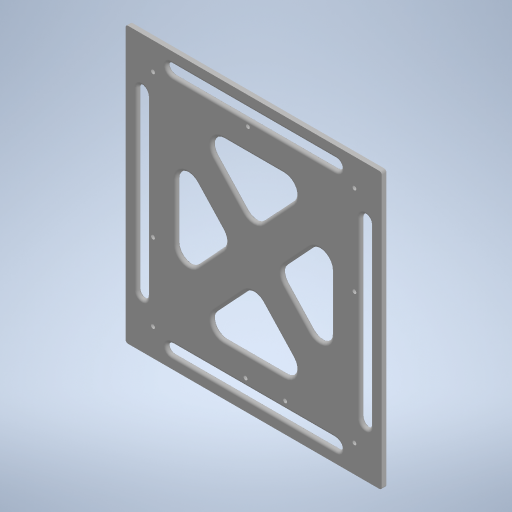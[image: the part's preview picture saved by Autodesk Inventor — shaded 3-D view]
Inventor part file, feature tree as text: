
AUTODESK INVENTOR PART (.ipt)
format: ipt  version: 2023 (Build 270158000, 158)  size: 484,352 bytes
history: native  units: in
note: dims shown in document units (in); Inventor stores cm internally (conversion verified against a paired STEP export)
features: fillet x5, sketch x3, extrude x2, hole x1
ambient origin geometry x8: Origin, YZ Plane, XZ Plane, XY Plane, X Axis, Y Axis, Z Axis, Center Point
bodies: Solid1 (feature_tree)
feature tree (11):
  extrude  "Extrusion1"  Depth=9.311in
  hole  "Hole1"  [1 undecoded]
  extrude  "Extrusion2"  Depth=0.0984in
  fillet  "Fillet1"  Radius=0.1378in
  fillet  "Fillet2"  Radius=0.1378in
  fillet  "Fillet3"  Radius=0.1378in
  fillet  "Fillet6"  Radius=2.7559in
  fillet  "Fillet7"  Radius=4.5669in
  sketch  "Sketch1"  dims[d1=8.6614in d2=9.311in]
  sketch  "Sketch2"  dims[d3=0.1575in d4=0.0in d5=7.0866in]
  sketch  "Sketch3"  dims[d6=7.7362in d7=0.1378in d8=0.1378in d10=0.1378in d11=0.1378in d12=2.7559in d13=4.5669in d16=3.3465in d17=0.1339in d18=0.2362in d19=0.1575in d20=0.0787in d21=90.0deg d22=0.315in d23=0.8108in d24=3.2681in d25=4.6063in d26=0.1969in d27=0.3937in d28=0.1969in d29=0.7874in d30=0.5906in d31=0.5906in d32=0.5906in d33=0.5906in d34=0.1575in d35=0.0in d36=0.3937in d37=0.2559in d38=0.0787in d41=0.1575in d42=0.0984in d40=0.0in d43=0.0in]
note: 1 required parameter value undecoded (feature->parameter linkage not recoverable at this tier; creation-order binding heuristic only, values carry confidence <= 0.55)
